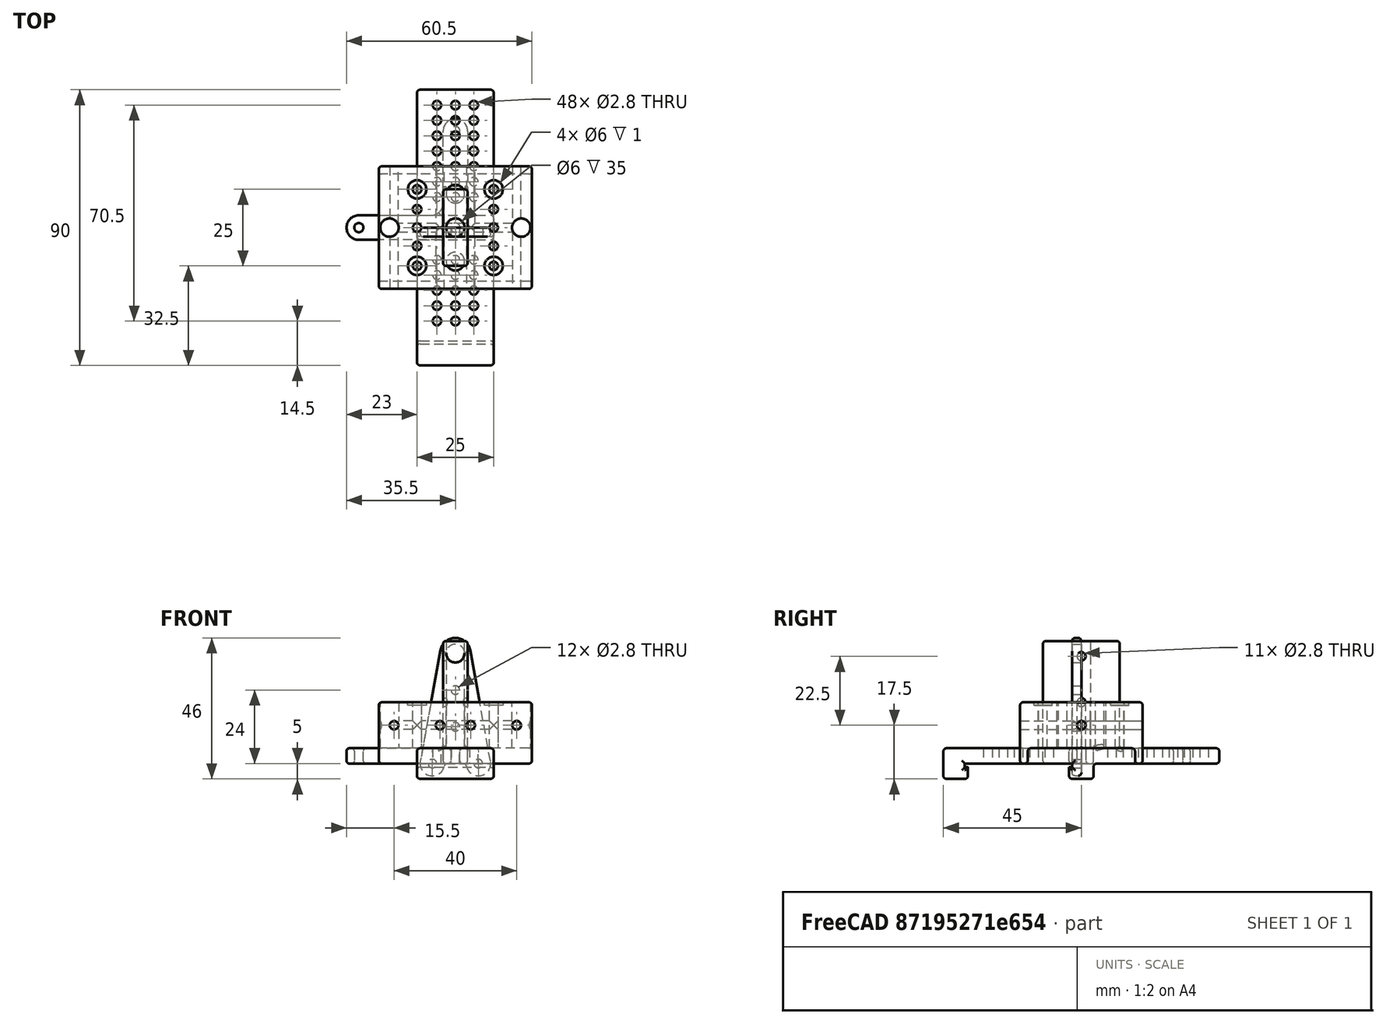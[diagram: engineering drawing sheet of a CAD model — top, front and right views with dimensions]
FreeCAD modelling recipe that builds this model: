
FCSTD DOCUMENT  (FreeCAD 1.1R39980 (Git))
Label: xy_switch
License: All rights reserved
LicenseURL: https://en.wikipedia.org/wiki/All_rights_reserved
objects: Sketcher::SketchObject×14, PartDesign::Pad×8, PartDesign::Pocket×7, App::Point×4, PartDesign::Fillet×4, PartDesign::Body×4, PartDesign::SubShapeBinder×2
note: 91 computed .brp shape members not serialized (recipe doc carries the construction recipe); baked Part::Feature solids carry a one-line shape summary decoded from their .brp

FEATURE [App::Point] Origin001
  Role = Origin
FEATURE [Sketcher::SketchObject] Sketch
  ArcFitTolerance = 1e-06
  AttachmentSupport = -> [XY_Plane]
  ExternalTypes = [0]
  FullyConstrained = true
  MakeInternals = false
  MapMode = 5
  sketch-geometry (4):
    g0: LineSegment StartX=-25 StartY=20 StartZ=0 EndX=-25 EndY=-20 EndZ=0
    g1: LineSegment StartX=-25 StartY=-20 StartZ=0 EndX=25 EndY=-20 EndZ=0
    g2: LineSegment StartX=25 StartY=-20 StartZ=0 EndX=25 EndY=20 EndZ=0
    g3: LineSegment StartX=25 StartY=20 StartZ=0 EndX=-25 EndY=20 EndZ=0
  constraints (11):
    c: Coincident(g0,g1)
    c: Coincident(g1,g2)
    c: Coincident(g2,g3)
    c: Coincident(g3,g0)
    c: Vertical(g0)
    c: Vertical(g2)
    c: Horizontal(g1)
    c: Horizontal(g3)
    c: Distance(g0,g2) = 50
    c: Distance(g1,g3) = 40
    c: Symmetric(g0,g2,g-1)
FEATURE [PartDesign::Pad] Pad
  Direction = (0,0,1)
  Length = 20
  Length2 = 10
  Profile = -> Sketch
  ReferenceAxis = -> Sketch [N_Axis]
  Refine = true
  Suppressed = false
  Type = 0
FEATURE [Sketcher::SketchObject] Sketch001
  ArcFitTolerance = 1e-06
  AttachmentSupport = -> [Pad]
  ExternalTypes = [0]
  FullyConstrained = true
  MakeInternals = false
  MapMode = 5
  Placement = pos=(25,0,0) rot=(0.57735,0.57735,0.57735;2.0944rad)
  sketch-geometry (4):
    g0: LineSegment StartX=-17.5 StartY=0 StartZ=0 EndX=17.5 EndY=1e-16 EndZ=0
    g1: LineSegment StartX=17.5 StartY=1e-16 StartZ=0 EndX=17.5 EndY=5 EndZ=0
    g2: LineSegment StartX=17.5 StartY=5 StartZ=0 EndX=-17.5 EndY=5 EndZ=0
    g3: LineSegment StartX=-17.5 StartY=5 StartZ=0 EndX=-17.5 EndY=0 EndZ=0
  constraints (11):
    c: Coincident(g0,g1)
    c: Coincident(g1,g2)
    c: Coincident(g2,g3)
    c: Coincident(g3,g0)
    c: Horizontal(g2)
    c: Vertical(g1)
    c: Vertical(g3)
    c: PointOnObject(g0,g-1)
    c: Symmetric(g0,g0,g-2)
    c: DistanceX(g0,g0) = 35
    c: Distance(g1,g1) = 5
FEATURE [PartDesign::Pocket] Pocket
  BaseFeature = -> Pad
  Direction = (-1,0,0)
  Length = 5
  Length2 = 5
  Profile = -> Sketch001
  ReferenceAxis = -> Sketch001 [N_Axis]
  Refine = true
  Suppressed = false
  Type = 1
FEATURE [Sketcher::SketchObject] Sketch002
  ArcFitTolerance = 1e-06
  AttachmentSupport = -> [Pocket]
  ExternalTypes = [0]
  FullyConstrained = false
  MakeInternals = false
  MapMode = 5
  Placement = pos=(0,0,20) rot=(0,0,1;0rad)
  sketch-geometry (16):
    g0: Circle CenterX=-12.5 CenterY=12.5 CenterZ=0 NormalX=0 NormalY=0 NormalZ=1 AngleXU=0 Radius=1.4
    g1: Circle CenterX=-12.5 CenterY=-12.5 CenterZ=0 NormalX=0 NormalY=0 NormalZ=1 AngleXU=0 Radius=1.4
    g2: Circle CenterX=12.5 CenterY=12.5 CenterZ=0 NormalX=0 NormalY=0 NormalZ=1 AngleXU=0 Radius=1.4
    g3: Circle CenterX=12.5 CenterY=-12.5 CenterZ=0 NormalX=0 NormalY=0 NormalZ=1 AngleXU=0 Radius=1.4
    g4: Circle CenterX=-12.5 CenterY=6 CenterZ=0 NormalX=0 NormalY=0 NormalZ=1 AngleXU=0 Radius=1.4
    g5: Circle CenterX=-12.5 CenterY=0 CenterZ=0 NormalX=0 NormalY=0 NormalZ=1 AngleXU=0 Radius=1.4
    g6: Circle CenterX=-12.5 CenterY=-6 CenterZ=0 NormalX=0 NormalY=0 NormalZ=1 AngleXU=0 Radius=1.4
    g7: Circle CenterX=12.5 CenterY=6 CenterZ=0 NormalX=0 NormalY=0 NormalZ=1 AngleXU=0 Radius=1.4
    g8: Circle CenterX=12.5 CenterY=0 CenterZ=0 NormalX=0 NormalY=0 NormalZ=1 AngleXU=0 Radius=1.4
    g9: Circle CenterX=12.5 CenterY=-6 CenterZ=0 NormalX=0 NormalY=0 NormalZ=1 AngleXU=0 Radius=1.4
    g10: LineSegment [constr] StartX=-12.5 StartY=14.77 StartZ=0 EndX=-12.5 EndY=-16.9703 EndZ=0
    g11: LineSegment [constr] StartX=12.5 StartY=14.5123 StartZ=0 EndX=12.5 EndY=-16.9703 EndZ=0
    g12: Circle CenterX=0 CenterY=11 CenterZ=0 NormalX=0 NormalY=0 NormalZ=1 AngleXU=0 Radius=3
    g13: Circle CenterX=0 CenterY=-11 CenterZ=0 NormalX=0 NormalY=0 NormalZ=1 AngleXU=0 Radius=3
    g14: Circle CenterX=-21.5 CenterY=0 CenterZ=0 NormalX=0 NormalY=0 NormalZ=1 AngleXU=0 Radius=3
    g15: Circle CenterX=21.5 CenterY=0 CenterZ=0 NormalX=0 NormalY=0 NormalZ=1 AngleXU=0 Radius=3
  constraints (41):
    c: PointOnObject(g5,g-1)
    c: PointOnObject(g8,g-1)
    c: Equal(g0,g4)
    c: Equal(g4,g5)
    c: Equal(g5,g6)
    c: Equal(g6,g1)
    c: Equal(g1,g3)
    c: Equal(g3,g9)
    c: Equal(g9,g8)
    c: Equal(g8,g7)
    c: Equal(g7,g2)
    c: Diameter(g0) = 2.8
    c: Vertical(g10)
    c: Vertical(g11)
    c: Symmetric(g10,g11,g-2)
    c: PointOnObject(g5,g10)
    c: PointOnObject(g8,g11)
    c: Symmetric(g6,g4,g-1)
    c: Symmetric(g9,g7,g-1)
    c: Symmetric(g0,g1,g-1)
    c: PointOnObject(g1,g10)
    c: PointOnObject(g6,g10)
    c: PointOnObject(g3,g11)
    c: PointOnObject(g9,g11)
    c: PointOnObject(g2,g11)
    c: Horizontal(g0,g2)
    c: Horizontal(g1,g3)
    c: Horizontal(g6,g9)
    c: DistanceY(g1,g0) = 25
    c: DistanceY(g9,g7) = 12
    c: DistanceX(g10,g11) = 25
    c: PointOnObject(g12,g-2)
    c: Symmetric(g12,g13,g-1)
    c: Equal(g13,g12)
    c: Diameter(g12) = 6
    c: Distance(g12,g13) = 22
    c: PointOnObject(g14,g-1)
    c: Equal(g14,g15)
    c: Equal(g15,g12)
    c: Symmetric(g14,g15,g-2)
    c: DistanceX(g14,g1) = 9
FEATURE [Sketcher::SketchObject] Sketch004
  ArcFitTolerance = 1e-06
  ExternalTypes = [0,0,0]
  FullyConstrained = false
  MakeInternals = false
  MapMode = 5
  Placement = pos=(0,20,0) rot=(0,0.707107,0.707107;3.14159rad)
  sketch-geometry (6):
    g0: Circle CenterX=5 CenterY=12.5 CenterZ=0 NormalX=0 NormalY=0 NormalZ=1 AngleXU=0 Radius=1.4
    g1: Circle CenterX=20 CenterY=12.5 CenterZ=0 NormalX=0 NormalY=0 NormalZ=1 AngleXU=0 Radius=1.4
    g2: Circle CenterX=-5 CenterY=12.5 CenterZ=0 NormalX=0 NormalY=0 NormalZ=1 AngleXU=0 Radius=1.4
    g3: Circle CenterX=-20 CenterY=12.5 CenterZ=0 NormalX=0 NormalY=0 NormalZ=1 AngleXU=0 Radius=1.4
    g4: LineSegment [constr] StartX=-20 StartY=12.5 StartZ=0 EndX=20 EndY=12.5 EndZ=0
    g5: LineSegment [constr] StartX=-12.5 StartY=26.6104 StartZ=0 EndX=-12.5 EndY=-8.49335 EndZ=0
  constraints (12):
    c: Coincident(g4,g3)
    c: Coincident(g1,g4)
    c: Equal(g3,g2)
    c: Equal(g2,g0)
    c: Equal(g0,g1)
    c: Diameter(g1) = 2.8
    c: Symmetric(g2,g0,g-2)
    c: Symmetric(g3,g1,g-2)
    c: DistanceX(g3,g2) = 15
    c: Symmetric(g-3,g-1,g5)
    c: Symmetric(g3,g2,g5)
    c: DistanceY(g3,g-3) = 7.5
FEATURE [Sketcher::SketchObject] Sketch005
  ArcFitTolerance = 1e-06
  ExternalTypes = [0]
  FullyConstrained = true
  MakeInternals = false
  MapMode = 5
  Placement = pos=(-25,0,0) rot=(0.57735,-0.57735,-0.57735;2.0944rad)
  sketch-geometry (1):
    g0: Circle CenterX=0 CenterY=12.5 CenterZ=0 NormalX=0 NormalY=0 NormalZ=1 AngleXU=0 Radius=1.4
  constraints (3):
    c: PointOnObject(g0,g-2)
    c: Diameter(g0) = 2.8
    c: DistanceY(g-1,g0) = 12.5
FEATURE [PartDesign::Fillet] Fillet
  Base = -> Pocket [Edge1,Edge2,Edge3,Edge4,Edge5,Edge6,Edge7,Edge8,Edge9,Edge10,Edge11,Edge12,Edge13,Edge14,Edge15,Edge16,Edge17,Edge18,Edge19,Edge20,Edge21,Edge22,Edge23,Edge24]
  BaseFeature = -> Pocket
  Radius = 1
  Refine = true
  SupportTransform = false
  Suppressed = false
  UseAllEdges = true
FEATURE [PartDesign::Pocket] Pocket004
  BaseFeature = -> Fillet
  Direction = (0,0,-1)
  Length = 5
  Length2 = 5
  Profile = -> Sketch002
  ReferenceAxis = -> Sketch002 [N_Axis]
  Refine = true
  Suppressed = false
  Type = 1
FEATURE [PartDesign::Pocket] Pocket005
  BaseFeature = -> Pocket004
  Direction = (0,-1,2e-16)
  Length = 5
  Length2 = 5
  Profile = -> Sketch004
  ReferenceAxis = -> Sketch004 [N_Axis]
  Refine = true
  Suppressed = false
  Type = 1
FEATURE [PartDesign::Pocket] Pocket006
  BaseFeature = -> Pocket005
  Direction = (1,0,0)
  Length = 5
  Length2 = 5
  Profile = -> Sketch005
  ReferenceAxis = -> Sketch005 [N_Axis]
  Refine = true
  Suppressed = false
  Type = 1
FEATURE [Sketcher::SketchObject] Sketch006
  ArcFitTolerance = 1e-06
  AttachmentSupport = -> [Pocket006]
  ExternalGeometry = -> [Pocket006]
  ExternalTypes = [0,0,0,0]
  FullyConstrained = true
  MakeInternals = false
  MapMode = 5
  Placement = pos=(0,0,20) rot=(0,0,1;0rad)
  sketch-geometry (4):
    g0: Circle CenterX=-12.5 CenterY=12.5 CenterZ=0 NormalX=0 NormalY=0 NormalZ=1 AngleXU=0 Radius=3
    g1: Circle CenterX=12.5 CenterY=12.5 CenterZ=0 NormalX=0 NormalY=0 NormalZ=1 AngleXU=0 Radius=3
    g2: Circle CenterX=12.5 CenterY=-12.5 CenterZ=0 NormalX=0 NormalY=0 NormalZ=1 AngleXU=0 Radius=3
    g3: Circle CenterX=-12.5 CenterY=-12.5 CenterZ=0 NormalX=0 NormalY=0 NormalZ=1 AngleXU=0 Radius=3
  constraints (8):
    c: Coincident(g0,g-3)
    c: Coincident(g1,g-6)
    c: Coincident(g2,g-5)
    c: Coincident(g3,g-4)
    c: Equal(g3,g2)
    c: Equal(g2,g1)
    c: Equal(g1,g0)
    c: Diameter(g1) = 6
FEATURE [PartDesign::Pocket] Pocket007
  BaseFeature = -> Pocket006
  Direction = (0,0,-1)
  Length = 1
  Length2 = 5
  Profile = -> Sketch006
  ReferenceAxis = -> Sketch006 [N_Axis]
  Refine = true
  Suppressed = false
  Type = 0
FEATURE [PartDesign::Body] Body
  AllowCompound = false
  Group = -> [Sketch,Pad,Sketch001,Pocket,Sketch002,Sketch004,Sketch005,Fillet,Pocket004,Pocket005,Pocket006,Sketch006,Pocket007]
  Origin = -> Origin
  Tip = -> Pocket007
FEATURE [App::Point] Origin003
  Role = Origin
FEATURE [Sketcher::SketchObject] Sketch007
  ArcFitTolerance = 1e-06
  AttachmentSupport = -> [XZ_Plane001]
  ExternalTypes = [0,0]
  FullyConstrained = true
  MakeInternals = false
  MapMode = 5
  Placement = pos=(0,0,0) rot=(1,0,0;1.5708rad)
  sketch-geometry (11):
    g0: Circle CenterX=7.5 CenterY=0 CenterZ=0 NormalX=0 NormalY=0 NormalZ=1 AngleXU=0 Radius=1.4
    g1: Circle CenterX=-7.5 CenterY=0 CenterZ=0 NormalX=0 NormalY=0 NormalZ=1 AngleXU=0 Radius=1.4
    g2: Circle CenterX=0 CenterY=36 CenterZ=0 NormalX=0 NormalY=0 NormalZ=1 AngleXU=0 Radius=3
    g3: ArcOfCircle CenterX=0 CenterY=36 CenterZ=0 NormalX=0 NormalY=0 NormalZ=1 AngleXU=0 Radius=5 StartAngle=0.178198 EndAngle=2.96339
    g4: ArcOfCircle CenterX=7.5 CenterY=0 CenterZ=0 NormalX=0 NormalY=0 NormalZ=1 AngleXU=0 Radius=4 StartAngle=3.14159 EndAngle=6.46138
    g5: ArcOfCircle CenterX=-7.5 CenterY=0 CenterZ=0 NormalX=0 NormalY=0 NormalZ=1 AngleXU=0 Radius=4 StartAngle=2.96339 EndAngle=6.28319
    g6: LineSegment StartX=-4.92082 StartY=36.8863 StartZ=0 EndX=-11.4367 EndY=0.709026 EndZ=0
    g7: LineSegment StartX=11.4367 StartY=0.709026 StartZ=0 EndX=4.92082 EndY=36.8863 EndZ=0
    g8: LineSegment StartX=3.5 StartY=5e-16 StartZ=0 EndX=-3.5 EndY=-1e-15 EndZ=0
    g9: Circle CenterX=0 CenterY=24 CenterZ=0 NormalX=0 NormalY=0 NormalZ=1 AngleXU=0 Radius=1.4
    g10: Circle CenterX=0 CenterY=12 CenterZ=0 NormalX=0 NormalY=0 NormalZ=1 AngleXU=0 Radius=1.4
  constraints (28):
    c: PointOnObject(g0,g-1)
    c: PointOnObject(g2,g-2)
    c: Equal(g0,g1)
    c: Diameter(g2) = 6
    c: Diameter(g0) = 2.8
    c: DistanceX(g1,g0) = 15
    c: Symmetric(g0,g1,g-2)
    c: DistanceY(g-1,g2) = 36
    c: Coincident(g3,g2)
    c: Coincident(g4,g0)
    c: Coincident(g5,g1)
    c: Equal(g4,g5)
    c: Tangent(g7,g3) = -1.5708
    c: Tangent(g6,g3) = -1.5708
    c: Tangent(g6,g5) = -1.5708
    c: Tangent(g7,g4) = -1.5708
    c: PointOnObject(g4,g-1)
    c: PointOnObject(g5,g-1)
    c: Coincident(g8,g4)
    c: Coincident(g8,g5)
    c: Radius(g3) = 5
    c: Radius(g5) = 4
    c: PointOnObject(g9,g-2)
    c: PointOnObject(g10,g-2)
    c: Equal(g10,g9)
    c: Equal(g9,g0)
    c: Distance(g-1,g10) = 12
    c: DistanceY(g10,g9) = 12
FEATURE [PartDesign::SubShapeBinder] Binder
  BindCopyOnChange = 0
  BindMode = 0
  ClaimChildren = false
  Context = -> Body001 [Binder.]
  Fuse = false
  MakeFace = true
  OffsetFill = false
  OffsetIntersection = false
  OffsetJoinType = 0
  OffsetOpenResult = false
  PartialLoad = false
  Refine = true
  Relative = true
  Support = -> [Body[Pocket007.Face24]]
  _Version = 2
FEATURE [PartDesign::Pad] Pad001
  Direction = (0,-1,2e-16)
  Length = 3
  Length2 = 10
  Placement = pos=(0,0,0) rot=(1,0,0;1.5708rad)
  Profile = -> Sketch007
  ReferenceAxis = -> Sketch007 [N_Axis]
  Refine = true
  Suppressed = false
  Type = 0
FEATURE [PartDesign::Fillet] Fillet001
  Base = -> Pad001 [Face2,Face6]
  BaseFeature = -> Pad001
  Placement = pos=(0,0,0) rot=(1,0,0;1.5708rad)
  Radius = 1
  Refine = true
  SupportTransform = false
  Suppressed = false
  UseAllEdges = false
FEATURE [PartDesign::Body] Body001
  AllowCompound = false
  Group = -> [Sketch007,Binder,Pad001,Fillet001]
  Origin = -> Origin002
  Tip = -> Fillet001
FEATURE [App::Point] Origin005
  Role = Origin
FEATURE [Sketcher::SketchObject] Sketch008
  ArcFitTolerance = 1e-06
  AttachmentSupport = -> [XY_Plane002]
  ExternalTypes = [0]
  FullyConstrained = true
  MakeInternals = false
  MapMode = 5
  sketch-geometry (12):
    g0: Circle CenterX=-31.5 CenterY=0 CenterZ=0 NormalX=0 NormalY=0 NormalZ=1 AngleXU=0 Radius=1.5
    g1: Circle CenterX=0 CenterY=0 CenterZ=0 NormalX=0 NormalY=0 NormalZ=1 AngleXU=0 Radius=1.5
    g2: Circle CenterX=0 CenterY=31.5 CenterZ=0 NormalX=0 NormalY=0 NormalZ=1 AngleXU=0 Radius=1.5
    g3: LineSegment [constr] StartX=-31.5 StartY=0 StartZ=0 EndX=0 EndY=0 EndZ=0
    g4: LineSegment [constr] StartX=0 StartY=0 StartZ=0 EndX=0 EndY=31.5 EndZ=0
    g5: ArcOfCircle CenterX=-8 CenterY=8 CenterZ=0 NormalX=0 NormalY=0 NormalZ=1 AngleXU=0 Radius=4 StartAngle=4.71239 EndAngle=6.28319
    g6: ArcOfCircle CenterX=-31.5 CenterY=0 CenterZ=0 NormalX=0 NormalY=0 NormalZ=1 AngleXU=0 Radius=4 StartAngle=1.5708 EndAngle=4.71239
    g7: ArcOfCircle CenterX=0 CenterY=31.5 CenterZ=0 NormalX=0 NormalY=0 NormalZ=1 AngleXU=0 Radius=4 StartAngle=0 EndAngle=3.14159
    g8: LineSegment StartX=4 StartY=31.5 StartZ=0 EndX=4 EndY=-4 EndZ=0
    g9: LineSegment StartX=4 StartY=-4 StartZ=0 EndX=-31.5 EndY=-4 EndZ=0
    g10: LineSegment StartX=-31.5 StartY=4 StartZ=0 EndX=-8 EndY=4 EndZ=0
    g11: LineSegment StartX=-4 StartY=8 StartZ=0 EndX=-4 EndY=31.5 EndZ=0
  constraints (28):
    c: PointOnObject(g0,g-1)
    c: Coincident(g1,g-1)
    c: PointOnObject(g2,g-2)
    c: Equal(g0,g1)
    c: Equal(g1,g2)
    c: Diameter(g2) = 3
    c: Coincident(g3,g0)
    c: Coincident(g3,g1)
    c: Coincident(g4,g1)
    c: Coincident(g4,g2)
    c: Equal(g4,g3)
    c: DistanceY(g4,g4) = 31.5
    c: Coincident(g6,g0)
    c: Coincident(g7,g2)
    c: Vertical(g8)
    c: Horizontal(g9)
    c: Tangent(g11,g7) = 1.5708
    c: Tangent(g9,g6) = 1.5708
    c: Tangent(g8,g7) = 1.5708
    c: Tangent(g11,g5) = -1.5708
    c: Tangent(g10,g5) = -1.5708
    c: Tangent(g10,g6) = 1.5708
    c: Parallel(g9,g10)
    c: Parallel(g11,g8)
    c: Equal(g7,g5)
    c: Coincident(g9,g8)
    c: DistanceY(g6,g6) = 8
    c: Distance(g7,g7) = 8
FEATURE [PartDesign::Pad] Pad002
  Direction = (0,0,1)
  Length = 5
  Length2 = 10
  Profile = -> Sketch008
  ReferenceAxis = -> Sketch008 [N_Axis]
  Refine = true
  Suppressed = false
  Type = 0
FEATURE [Sketcher::SketchObject] Sketch009
  ArcFitTolerance = 1e-06
  AttachmentSupport = -> [Pad002]
  ExternalGeometry = -> [Pad002]
  ExternalTypes = [0,0]
  FullyConstrained = false
  MakeInternals = false
  MapMode = 5
  Placement = pos=(0,0,5) rot=(0,0,1;0rad)
  sketch-geometry (14):
    g0: LineSegment StartX=3 StartY=12.5 StartZ=0 EndX=-3 EndY=12.5 EndZ=0
    g1: LineSegment StartX=-4 StartY=11.5 StartZ=0 EndX=-4 EndY=4.7697 EndZ=0
    g2: LineSegment StartX=-3 StartY=-12.5 StartZ=0 EndX=3 EndY=-12.5 EndZ=0
    g3: LineSegment StartX=4 StartY=-11.5 StartZ=0 EndX=4 EndY=11.5 EndZ=0
    g4: LineSegment StartX=-4 StartY=4.7697 StartZ=0 EndX=-4 EndY=-11.5 EndZ=0
    g5: ArcOfCircle CenterX=3 CenterY=11.5 CenterZ=0 NormalX=0 NormalY=0 NormalZ=1 AngleXU=0 Radius=1 StartAngle=-9e-16 EndAngle=1.5708
    g6: GeomPoint [constr] X=4 Y=12.5 Z=0
    g7: ArcOfCircle CenterX=-3 CenterY=11.5 CenterZ=0 NormalX=0 NormalY=0 NormalZ=1 AngleXU=0 Radius=1 StartAngle=1.5708 EndAngle=3.14159
    g8: GeomPoint [constr] X=-4 Y=12.5 Z=0
    g9: ArcOfCircle CenterX=-3 CenterY=-11.5 CenterZ=0 NormalX=0 NormalY=0 NormalZ=1 AngleXU=0 Radius=1 StartAngle=3.14159 EndAngle=4.71239
    g10: GeomPoint [constr] X=-4 Y=-12.5 Z=0
    g11: ArcOfCircle CenterX=3 CenterY=-11.5 CenterZ=0 NormalX=0 NormalY=0 NormalZ=1 AngleXU=0 Radius=1 StartAngle=4.71239 EndAngle=6.28319
    g12: GeomPoint [constr] X=4 Y=-12.5 Z=0
    g13: Circle CenterX=0 CenterY=0 CenterZ=0 NormalX=0 NormalY=0 NormalZ=1 AngleXU=0 Radius=3
  constraints (31):
    c: Horizontal(g0)
    c: Horizontal(g2)
    c: Distance(g8,g6) = 8
    c: Distance(g6,g12) = 25
    c: PointOnObject(g6,g-3)
    c: Vertical(g1)
    c: Vertical(g4)
    c: Vertical(g10,g1)
    c: Symmetric(g12,g6,g-1)
    c: PointOnObject(g6,g0)
    c: PointOnObject(g6,g3)
    c: Tangent(g0,g5) = -1.5708
    c: Tangent(g3,g5) = -1.5708
    c: PointOnObject(g8,g0)
    c: PointOnObject(g8,g1)
    c: Tangent(g0,g7) = -1.5708
    c: Tangent(g1,g7) = -1.5708
    c: PointOnObject(g10,g2)
    c: Tangent(g4,g9) = -1.5708
    c: Tangent(g2,g9) = -1.5708
    c: PointOnObject(g12,g2)
    c: PointOnObject(g12,g3)
    c: Tangent(g2,g11) = -1.5708
    c: Tangent(g3,g11) = -1.5708
    c: Equal(g11,g9)
    c: Equal(g9,g7)
    c: Equal(g7,g5)
    c: Radius(g7) = 1
    c: Coincident(g1,g4)
    c: Diameter(g13) = 6
    c: Coincident(g13,g-1)
FEATURE [PartDesign::Pad] Pad003
  BaseFeature = -> Pad002
  Direction = (0,0,1)
  Length = 35
  Length2 = 5
  Profile = -> Sketch009
  ReferenceAxis = -> Sketch009 [N_Axis]
  Refine = true
  Suppressed = false
  Type = 4
FEATURE [Sketcher::SketchObject] Sketch010
  ArcFitTolerance = 1e-06
  AttachmentSupport = -> [Pad003]
  ExternalGeometry = -> [Pad003]
  ExternalTypes = [0]
  FullyConstrained = true
  MakeInternals = false
  MapMode = 5
  Placement = pos=(4,0,0) rot=(0.57735,0.57735,0.57735;2.0944rad)
  sketch-geometry (2):
    g0: Circle CenterX=0 CenterY=35 CenterZ=0 NormalX=0 NormalY=0 NormalZ=1 AngleXU=0 Radius=1.4
    g1: Circle CenterX=0 CenterY=20 CenterZ=0 NormalX=0 NormalY=0 NormalZ=1 AngleXU=0 Radius=1.4
  constraints (6):
    c: PointOnObject(g0,g-2)
    c: PointOnObject(g1,g-2)
    c: Equal(g0,g1)
    c: Diameter(g1) = 2.8
    c: DistanceY(g1,g0) = 15
    c: DistanceY(g0,g-3) = 5
FEATURE [PartDesign::Pocket] Pocket008
  BaseFeature = -> Pad003
  Direction = (-1,0,0)
  Length = 5
  Length2 = 5
  Profile = -> Sketch010
  ReferenceAxis = -> Sketch010 [N_Axis]
  Refine = true
  Suppressed = false
  Type = 1
FEATURE [PartDesign::Fillet] Fillet002
  Base = -> Pocket008 [Face4,Edge25,Edge22,Edge23,Edge52,Edge27,Edge29,Edge24,Edge50]
  BaseFeature = -> Pocket008
  Radius = 0.9
  Refine = true
  SupportTransform = false
  Suppressed = false
  UseAllEdges = false
FEATURE [PartDesign::Body] Body002
  AllowCompound = false
  Group = -> [Sketch008,Pad002,Sketch009,Pad003,Sketch010,Pocket008,Fillet002]
  Origin = -> Origin004
  Tip = -> Fillet002
FEATURE [App::Point] Origin007
  Role = Origin
FEATURE [Sketcher::SketchObject] Sketch011
  ArcFitTolerance = 1e-06
  AttachmentSupport = -> [XY_Plane003]
  ExternalTypes = [0]
  FullyConstrained = true
  MakeInternals = false
  MapMode = 5
  sketch-geometry (5):
    g0: LineSegment StartX=-12.5 StartY=-45 StartZ=0 EndX=12.5 EndY=-45 EndZ=0
    g1: LineSegment StartX=12.5 StartY=-45 StartZ=0 EndX=12.5 EndY=45 EndZ=0
    g2: LineSegment StartX=12.5 StartY=45 StartZ=0 EndX=-12.5 EndY=45 EndZ=0
    g3: LineSegment StartX=-12.5 StartY=45 StartZ=0 EndX=-12.5 EndY=-45 EndZ=0
    g4: GeomPoint [constr] X=0 Y=0 Z=0
  constraints (12):
    c: Coincident(g0,g1)
    c: Coincident(g1,g2)
    c: Coincident(g2,g3)
    c: Coincident(g3,g0)
    c: Horizontal(g0)
    c: Horizontal(g2)
    c: Vertical(g1)
    c: Vertical(g3)
    c: Symmetric(g2,g0,g4)
    c: Distance(g1,g3) = 25
    c: Distance(g0,g2) = 90
    c: Coincident(g4,g-1)
FEATURE [PartDesign::Pad] Pad004
  Direction = (0,0,1)
  Length = 5
  Length2 = 10
  Profile = -> Sketch011
  ReferenceAxis = -> Sketch011 [N_Axis]
  Refine = true
  Suppressed = false
  Type = 0
FEATURE [Sketcher::SketchObject] Sketch012
  ArcFitTolerance = 1e-06
  AttachmentSupport = -> [Pad004]
  ExternalGeometry = -> [Pad004]
  ExternalTypes = [0]
  FullyConstrained = true
  MakeInternals = false
  MapMode = 5
  Placement = pos=(0,0,0) rot=(1,0,0;3.14159rad)
  sketch-geometry (7):
    g0: LineSegment StartX=-12.5 StartY=45 StartZ=0 EndX=-12.5 EndY=38 EndZ=0
    g1: LineSegment StartX=-12.5 StartY=38 StartZ=0 EndX=12.5 EndY=38 EndZ=0
    g2: LineSegment StartX=12.5 StartY=38 StartZ=0 EndX=12.5 EndY=45 EndZ=0
    g3: LineSegment StartX=-12.5 StartY=3 StartZ=0 EndX=-12.5 EndY=-4 EndZ=0
    g4: LineSegment StartX=-12.5 StartY=-4 StartZ=0 EndX=12.5 EndY=-4 EndZ=0
    g5: LineSegment StartX=12.5 StartY=-4 StartZ=0 EndX=12.5 EndY=3 EndZ=0
    g6: LineSegment StartX=12.5 StartY=3 StartZ=0 EndX=-12.5 EndY=3 EndZ=0
  constraints (20):
    c: Coincident(g-3,g0)
    c: Coincident(g0,g1)
    c: Horizontal(g1)
    c: Coincident(g1,g2)
    c: Coincident(g2,g-3)
    c: Vertical(g0)
    c: Vertical(g2)
    c: Coincident(g3,g4)
    c: Coincident(g4,g5)
    c: Coincident(g5,g6)
    c: Coincident(g6,g3)
    c: Vertical(g3)
    c: Vertical(g5)
    c: Horizontal(g4)
    c: Horizontal(g6)
    c: Vertical(g5,g1)
    c: Vertical(g3,g0)
    c: Equal(g5,g2)
    c: DistanceY(g5,g1) = 35
    c: Distance(g2,g2) = 7
FEATURE [PartDesign::Pad] Pad005
  BaseFeature = -> Pad004
  Direction = (0,0,-1)
  Length = 5
  Length2 = 10
  Profile = -> Sketch012
  ReferenceAxis = -> Sketch012 [N_Axis]
  Refine = true
  Suppressed = false
  Type = 0
FEATURE [Sketcher::SketchObject] Sketch013
  ArcFitTolerance = 1e-06
  AttachmentSupport = -> [Pad005]
  ExternalGeometry = -> [Pad005]
  ExternalTypes = [0,0,0]
  FullyConstrained = true
  MakeInternals = false
  MapMode = 5
  Placement = pos=(0,0,0) rot=(1,0,0;3.14159rad)
  sketch-geometry (36):
    g0: Circle CenterX=-6 CenterY=-40 CenterZ=0 NormalX=0 NormalY=0 NormalZ=1 AngleXU=0 Radius=1.4
    g1: Circle CenterX=6 CenterY=-40 CenterZ=0 NormalX=0 NormalY=0 NormalZ=1 AngleXU=0 Radius=1.4
    g2: Circle CenterX=-6 CenterY=-35 CenterZ=0 NormalX=0 NormalY=0 NormalZ=1 AngleXU=0 Radius=1.4
    g3: Circle CenterX=6 CenterY=-35 CenterZ=0 NormalX=0 NormalY=0 NormalZ=1 AngleXU=0 Radius=1.4
    g4: Circle CenterX=-6 CenterY=-30 CenterZ=0 NormalX=0 NormalY=0 NormalZ=1 AngleXU=0 Radius=1.4
    g5: Circle CenterX=6 CenterY=-30 CenterZ=0 NormalX=0 NormalY=0 NormalZ=1 AngleXU=0 Radius=1.4
    g6: Circle CenterX=-6 CenterY=-10 CenterZ=0 NormalX=0 NormalY=0 NormalZ=1 AngleXU=0 Radius=1.4
    g7: Circle CenterX=6 CenterY=-10 CenterZ=0 NormalX=0 NormalY=0 NormalZ=1 AngleXU=0 Radius=1.4
    g8: Circle CenterX=-6 CenterY=-15 CenterZ=0 NormalX=0 NormalY=0 NormalZ=1 AngleXU=0 Radius=1.4
    g9: Circle CenterX=6 CenterY=-15 CenterZ=0 NormalX=0 NormalY=0 NormalZ=1 AngleXU=0 Radius=1.4
    g10: Circle CenterX=-6 CenterY=-20 CenterZ=0 NormalX=0 NormalY=0 NormalZ=1 AngleXU=0 Radius=1.4
    g11: Circle CenterX=6 CenterY=-20 CenterZ=0 NormalX=0 NormalY=0 NormalZ=1 AngleXU=0 Radius=1.4
    g12: Circle CenterX=-6 CenterY=-25 CenterZ=0 NormalX=0 NormalY=0 NormalZ=1 AngleXU=0 Radius=1.4
    g13: Circle CenterX=6 CenterY=-25 CenterZ=0 NormalX=0 NormalY=0 NormalZ=1 AngleXU=0 Radius=1.4
    g14: Circle CenterX=0 CenterY=-40 CenterZ=0 NormalX=0 NormalY=0 NormalZ=1 AngleXU=0 Radius=1.4
    g15: Circle CenterX=0 CenterY=-35 CenterZ=0 NormalX=0 NormalY=0 NormalZ=1 AngleXU=0 Radius=1.4
    g16: Circle CenterX=0 CenterY=-30 CenterZ=0 NormalX=0 NormalY=0 NormalZ=1 AngleXU=0 Radius=1.4
    g17: Circle CenterX=0 CenterY=-25 CenterZ=0 NormalX=0 NormalY=0 NormalZ=1 AngleXU=0 Radius=1.4
    g18: Circle CenterX=0 CenterY=-20 CenterZ=0 NormalX=0 NormalY=0 NormalZ=1 AngleXU=0 Radius=1.4
    g19: Circle CenterX=0 CenterY=-15 CenterZ=0 NormalX=0 NormalY=0 NormalZ=1 AngleXU=0 Radius=1.4
    g20: Circle CenterX=0 CenterY=-10 CenterZ=0 NormalX=0 NormalY=0 NormalZ=1 AngleXU=0 Radius=1.4
    g21: Circle CenterX=-6 CenterY=30.5 CenterZ=0 NormalX=0 NormalY=0 NormalZ=1 AngleXU=0 Radius=1.4
    g22: Circle CenterX=0 CenterY=30.5 CenterZ=0 NormalX=0 NormalY=0 NormalZ=1 AngleXU=0 Radius=1.4
    g23: Circle CenterX=6 CenterY=30.5 CenterZ=0 NormalX=0 NormalY=0 NormalZ=1 AngleXU=0 Radius=1.4
    g24: Circle CenterX=-6 CenterY=25.5 CenterZ=0 NormalX=0 NormalY=0 NormalZ=1 AngleXU=0 Radius=1.4
    g25: Circle CenterX=0 CenterY=25.5 CenterZ=0 NormalX=0 NormalY=0 NormalZ=1 AngleXU=0 Radius=1.4
    g26: Circle CenterX=6 CenterY=25.5 CenterZ=0 NormalX=0 NormalY=0 NormalZ=1 AngleXU=0 Radius=1.4
    g27: Circle CenterX=-6 CenterY=20.5 CenterZ=0 NormalX=0 NormalY=0 NormalZ=1 AngleXU=0 Radius=1.4
    g28: Circle CenterX=-3e-16 CenterY=20.5 CenterZ=0 NormalX=0 NormalY=0 NormalZ=1 AngleXU=0 Radius=1.4
    g29: Circle CenterX=6 CenterY=20.5 CenterZ=0 NormalX=0 NormalY=0 NormalZ=1 AngleXU=0 Radius=1.4
    g30: Circle CenterX=-6 CenterY=15.5 CenterZ=0 NormalX=0 NormalY=0 NormalZ=1 AngleXU=0 Radius=1.4
    g31: Circle CenterX=0 CenterY=15.5 CenterZ=0 NormalX=0 NormalY=0 NormalZ=1 AngleXU=0 Radius=1.4
    g32: Circle CenterX=6 CenterY=15.5 CenterZ=0 NormalX=0 NormalY=0 NormalZ=1 AngleXU=0 Radius=1.4
    g33: Circle CenterX=-6 CenterY=10.5 CenterZ=0 NormalX=0 NormalY=0 NormalZ=1 AngleXU=0 Radius=1.4
    g34: Circle CenterX=0 CenterY=10.5 CenterZ=0 NormalX=0 NormalY=0 NormalZ=1 AngleXU=0 Radius=1.4
    g35: Circle CenterX=6 CenterY=10.5 CenterZ=0 NormalX=0 NormalY=0 NormalZ=1 AngleXU=0 Radius=1.4
  constraints (95):
    c: Equal(g1,g0)
    c: Symmetric(g0,g1,g-2)
    c: Diameter(g1) = 2.8
    c: DistanceX(g0,g1) = 12
    c: DistanceY(g-3,g1) = 5
    c: Symmetric(g4,g5,g-2)
    c: Symmetric(g2,g3,g-2)
    c: Equal(g4,g2)
    c: Equal(g2,g3)
    c: Equal(g3,g5)
    c: Equal(g5,g1)
    c: Vertical(g0,g2)
    c: Vertical(g2,g4)
    c: DistanceY(g0,g2) = 5
    c: DistanceY(g2,g4) = 5
    c: PointOnObject(g14,g-2)
    c: PointOnObject(g15,g-2)
    c: PointOnObject(g16,g-2)
    c: PointOnObject(g17,g-2)
    c: PointOnObject(g18,g-2)
    c: PointOnObject(g19,g-2)
    c: PointOnObject(g20,g-2)
    c: PointOnObject(g22,g-2)
    c: PointOnObject(g25,g-2)
    c: PointOnObject(g31,g-2)
    c: PointOnObject(g34,g-2)
    c: Equal(g21,g22)
    c: Equal(g22,g23)
    c: Equal(g23,g26)
    c: Equal(g26,g25)
    c: Equal(g25,g24)
    c: Equal(g24,g27)
    c: Equal(g27,g28)
    c: Equal(g28,g29)
    c: Equal(g29,g32)
    c: Equal(g32,g31)
    c: Equal(g31,g30)
    c: Equal(g30,g33)
    c: Equal(g33,g34)
    c: Equal(g34,g35)
    c: Equal(g6,g20)
    c: Equal(g20,g7)
    c: Equal(g7,g9)
    c: Equal(g9,g19)
    c: Equal(g19,g8)
    c: Equal(g8,g10)
    c: Equal(g10,g18)
    c: Equal(g18,g11)
    c: Equal(g11,g13)
    c: Equal(g13,g17)
    c: Equal(g17,g12)
    c: Equal(g12,g16)
    c: Equal(g16,g15)
    c: Equal(g15,g14)
    c: Equal(g14,g5)
    c: Horizontal(g0,g14)
    c: Horizontal(g2,g15)
    c: Horizontal(g4,g16)
    c: Symmetric(g12,g13,g-2)
    c: Symmetric(g10,g11,g-2)
    c: Symmetric(g8,g9,g-2)
    c: Symmetric(g33,g35,g-2)
    c: Symmetric(g30,g32,g-2)
    c: Symmetric(g27,g29,g-2)
    c: Symmetric(g24,g26,g-2)
    c: Symmetric(g21,g23,g-2)
    c: Horizontal(g21,g22)
    c: Horizontal(g24,g25)
    c: Horizontal(g27,g28)
    c: Horizontal(g30,g31)
    c: Horizontal(g33,g34)
    c: Horizontal(g6,g20)
    c: Horizontal(g8,g19)
    c: Horizontal(g10,g18)
    c: Horizontal(g12,g17)
    c: DistanceY(g4,g12) = 5
    c: DistanceY(g12,g10) = 5
    c: DistanceY(g10,g8) = 5
    c: DistanceY(g8,g6) = 5
    c: Symmetric(g6,g7,g-2)
    c: Symmetric(g-4,g-5,g28)
    c: Vertical(g5,g13)
    c: Vertical(g13,g11)
    c: Vertical(g11,g9)
    c: Vertical(g9,g7)
    c: Vertical(g7,g35)
    c: Vertical(g35,g32)
    c: Vertical(g32,g29)
    c: Vertical(g29,g26)
    c: Vertical(g26,g23)
    c: Diameter(g23) = 2.8
    c: DistanceY(g27,g24) = 5
    c: DistanceY(g24,g21) = 5
    c: DistanceY(g30,g27) = 5
    c: DistanceY(g33,g30) = 5
FEATURE [PartDesign::Pocket] Pocket009
  BaseFeature = -> Pad005
  Direction = (0,0,1)
  Length = 5
  Length2 = 5
  Profile = -> Sketch013
  ReferenceAxis = -> Sketch013 [N_Axis]
  Refine = true
  Suppressed = false
  Type = 1
FEATURE [Sketcher::SketchObject] Sketch014
  ArcFitTolerance = 1e-06
  AttachmentSupport = -> [Pocket009]
  ExternalTypes = [0]
  FullyConstrained = true
  MakeInternals = false
  MapMode = 5
  Placement = pos=(0,-38,0) rot=(0,0.707107,0.707107;3.14159rad)
  sketch-geometry (4):
    g0: LineSegment StartX=-12.5 StartY=-1.2 StartZ=0 EndX=-12.5 EndY=-5 EndZ=0
    g1: LineSegment StartX=-12.5 StartY=-5 StartZ=0 EndX=12.5 EndY=-5 EndZ=0
    g2: LineSegment StartX=12.5 StartY=-5 StartZ=0 EndX=12.5 EndY=-1.2 EndZ=0
    g3: LineSegment StartX=12.5 StartY=-1.2 StartZ=0 EndX=-12.5 EndY=-1.2 EndZ=0
  constraints (11):
    c: Coincident(g0,g1)
    c: Coincident(g1,g2)
    c: Coincident(g2,g3)
    c: Coincident(g3,g0)
    c: Vertical(g0)
    c: Vertical(g2)
    c: Horizontal(g3)
    c: Distance(g0,g2) = 25
    c: Symmetric(g0,g1,g-2)
    c: DistanceY(g2,g-1) = 1.2
    c: DistanceY(g2,g2) = 3.8
FEATURE [PartDesign::Pad] Pad006
  BaseFeature = -> Pocket009
  Direction = (0,1,-2e-16)
  Length = 1
  Length2 = 10
  Profile = -> Sketch014
  ReferenceAxis = -> Sketch014 [N_Axis]
  Refine = true
  Suppressed = false
  Type = 0
FEATURE [PartDesign::SubShapeBinder] Binder001
  BindCopyOnChange = 0
  BindMode = 0
  ClaimChildren = false
  Context = -> Body003 [Binder001.]
  Fuse = false
  MakeFace = true
  OffsetFill = false
  OffsetIntersection = false
  OffsetJoinType = 0
  OffsetOpenResult = false
  PartialLoad = false
  Placement = pos=(0,35,0) rot=(0,0,1;0rad)
  Refine = true
  Relative = true
  Support = -> [Sketch014]
  _Version = 2
FEATURE [PartDesign::Pad] Pad007
  BaseFeature = -> Pad006
  Direction = (0,1,0)
  Length = 1
  Length2 = 10
  Profile = -> Binder001
  Refine = true
  Reversed = true
  Suppressed = false
  Type = 0
FEATURE [PartDesign::Fillet] Fillet003
  Base = -> Pad007 [Face50,Face51,Face42,Face52,Face5,Face44,Face4]
  BaseFeature = -> Pad007
  Radius = 1
  Refine = true
  SupportTransform = false
  Suppressed = false
  UseAllEdges = false
FEATURE [PartDesign::Body] Body003
  AllowCompound = false
  Group = -> [Sketch011,Pad004,Sketch012,Pad005,Sketch013,Pocket009,Sketch014,Pad006,Binder001,Pad007,Fillet003]
  Origin = -> Origin006
  Tip = -> Fillet003
